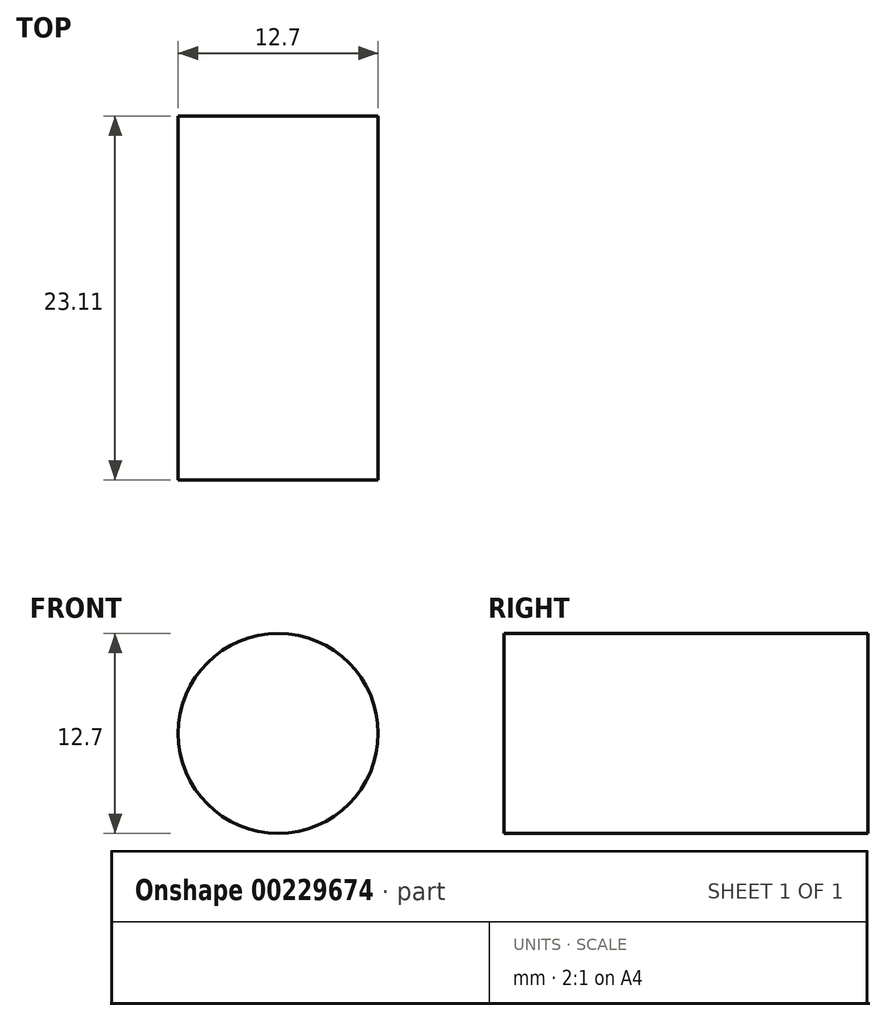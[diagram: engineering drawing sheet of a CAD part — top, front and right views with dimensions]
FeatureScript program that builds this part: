
annotation { "Feature Type Name" : "Feature", "Feature Type Description" : "" }
export const myFeature = defineFeature(function(context is Context, id is Id, definition is map)
    precondition{}
    {
        {
            var Q0;
            Q0=qCreatedBy(makeId("Front.planeOp"),FACE);
            var sketch = newSketch(context, id + "F0", { "sketchPlane" : qUnion([Q0])});
            skCircle(sketch, "E0", {"center": v(0, 0) * mm, "radius": 6.35 * mm});
            skSolve(sketch);
        }
        {
            var Q0;
            Q0 = qSketchRegion(id + "F0", true);
            extrude(context, id + "F1", {"entities" : qUnion([Q0]), "depth" : 23.1 * mm});
        }
    });
